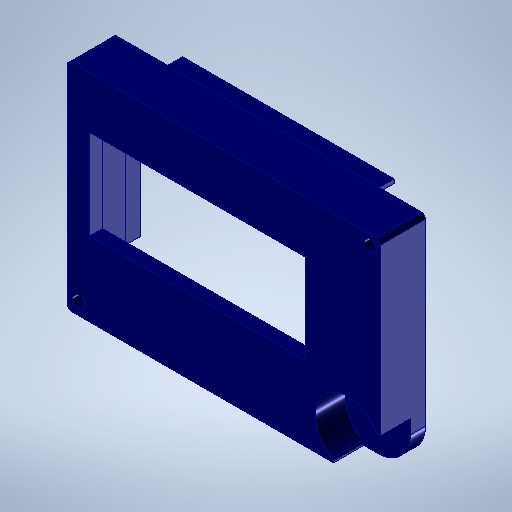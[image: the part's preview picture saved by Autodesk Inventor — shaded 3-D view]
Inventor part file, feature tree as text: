
AUTODESK INVENTOR PART (.ipt)
format: ipt  version: 2025.2 (Build 292293000, 293)  size: 745,984 bytes
history: native  units: mm
features: sketch x13, extrude x8, projected_geometry x8, fillet x2, hole x2, other x1
ambient origin geometry x8: Origin, YZ Plane, XZ Plane, XY Plane, X Axis, Y Axis, Z Axis, Center Point
bodies: Body1 (feature_tree)
feature tree (34):
  other  "Těleso1"
  extrude  "Vysunutí1"  Depth=30.0mm
  extrude  "Vysunutí2"  Depth=21.0mm TaperAngle=0.0deg
  extrude  "Vysunutí3"  Depth=14.0mm TaperAngle=0.0deg
  fillet  "Zaoblení1"  Radius=8.5mm
  fillet  "Zaoblení2"  Radius=12.0mm
  sketch  "Náčrt4"
  extrude  "Vysunutí4"  Depth=2.0mm
  extrude  "Vysunutí5"  Depth=1.5mm
  extrude  "Vysunutí6"  Depth=1.5mm
  sketch  "Náčrt8"
  extrude  "Vysunutí7"  Depth=1.0mm
  sketch  "Náčrt10"
  hole  "Díra1"  [1 undecoded]
  hole  "Díra2"  [1 undecoded]
  extrude  "Vysunutí8"  Depth=6.0mm
  sketch  "Náčrt1"
  sketch  "Náčrt2"
  projected_geometry  "Promítnutá smyčka1"
  sketch  "Náčrt3"
  projected_geometry  "Promítnutá smyčka2"
  projected_geometry  "Promítnutá smyčka3"
  sketch  "Náčrt5"
  sketch  "Náčrt6"
  projected_geometry  "Promítnutá smyčka4"
  sketch  "Náčrt7"
  projected_geometry  "Promítnutá smyčka5"
  projected_geometry  "Promítnutá smyčka6"
  sketch  "Náčrt9"
  projected_geometry  "Promítnutá smyčka7"
  sketch  "Náčrt11"
  sketch  "Náčrt12"
  projected_geometry  "Promítnutá smyčka8"
  sketch  "Náčrt13"
note: 2 required parameter values undecoded (feature->parameter linkage not recoverable at this tier; creation-order binding heuristic only, values carry confidence <= 0.55)
